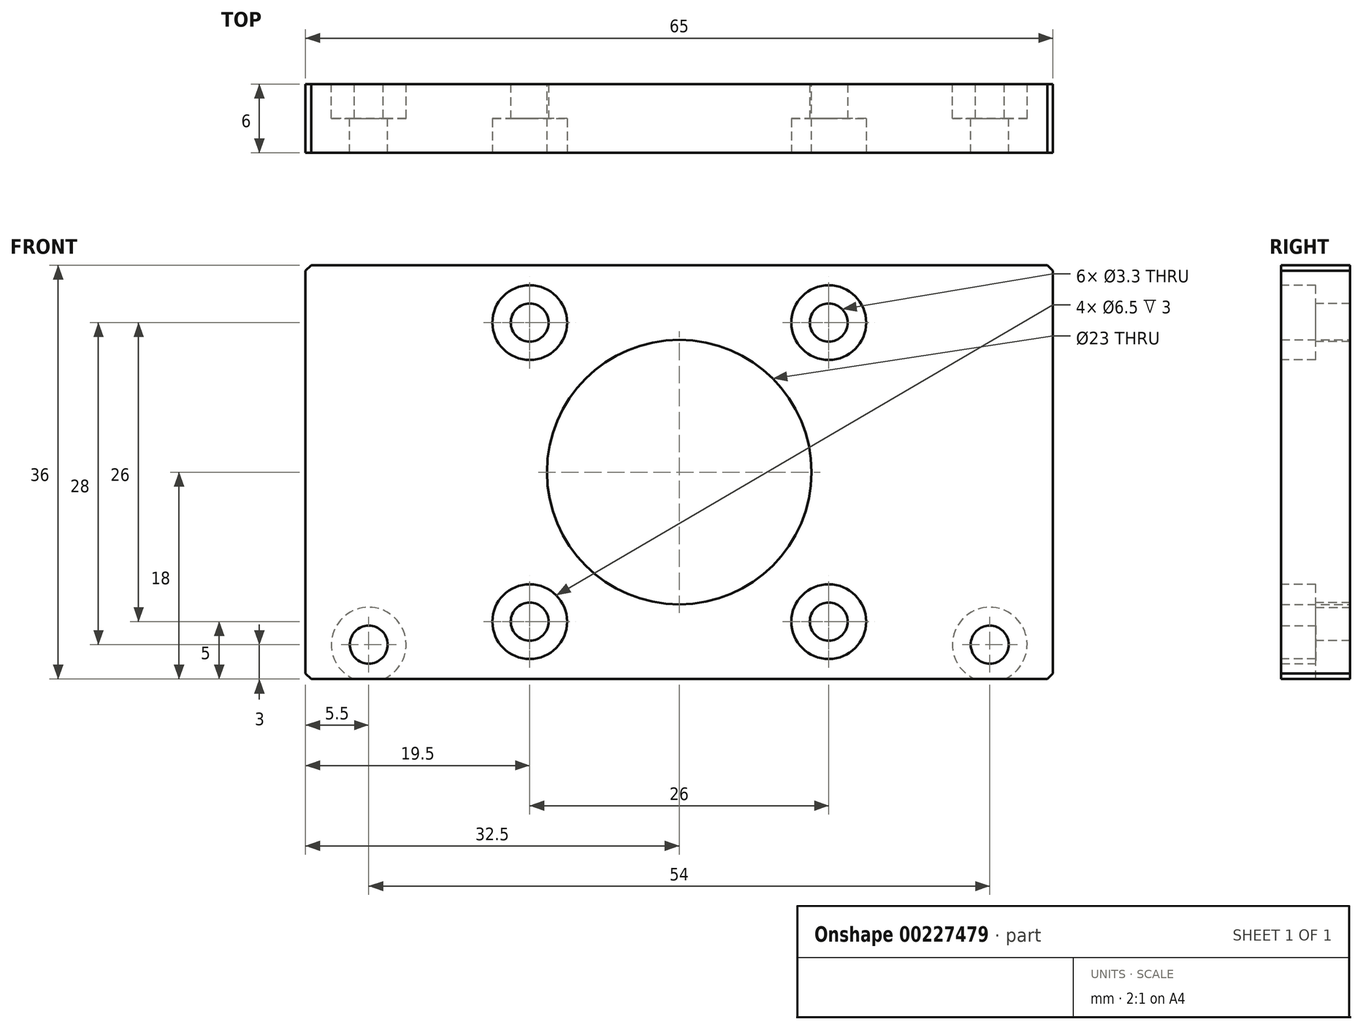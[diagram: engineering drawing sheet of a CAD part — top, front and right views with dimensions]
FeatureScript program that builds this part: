
annotation { "Feature Type Name" : "Feature", "Feature Type Description" : "" }
export const myFeature = defineFeature(function(context is Context, id is Id, definition is map)
    precondition{}
    {
        {
            var Q0;
            Q0=qCreatedBy(makeId("Front.planeOp"),FACE);
            var sketch = newSketch(context, id + "F0", { "sketchPlane" : qUnion([Q0])});
            skLineSegment(sketch, "E0.bottom", {"start": v(32.5, -18) * mm, "end": v(-32.5, -18) * mm});
            skLineSegment(sketch, "E0.top", {"start": v(32.5, 18) * mm, "end": v(-32.5, 18) * mm});
            skLineSegment(sketch, "E0.left", {"start": v(32.5, -18) * mm, "end": v(32.5, 18) * mm});
            skLineSegment(sketch, "E0.right", {"start": v(-32.5, -18) * mm, "end": v(-32.5, 18) * mm});
            skPoint(sketch, "E0.middle", {"position": v(0, 0) * mm});
            skCircle(sketch, "E1", {"center": v(0, 0) * mm, "radius": 11.5 * mm});
            skSolve(sketch);
        }
        {
            var Q0;
            Q0=makeQuery(id+"F0.imprint","IMPRINT",FACE,{"disambiguationData":[TD([[makeQuery(id+"F0.imprint","IMPRINT",EDGE,{"derivedFrom":sQuery(id+"F0.wireOp",EDGE,"E0.bottom")}),-1.0]])]});
            extrude(context, id + "F1", {"entities" : qUnion([Q0]), "depth" : 6 * mm});
        }
        {
            var Q0;
            Q0=makeQuery(id+"F1.opExtrude","CAP_FACE",FACE,{"disambiguationData":[OSD([sQuery(id+"F0.wireOp",EDGE,"E0.bottom"),sQuery(id+"F0.wireOp",EDGE,"E0.top"),sQuery(id+"F0.wireOp",EDGE,"E0.left"),sQuery(id+"F0.wireOp",EDGE,"E0.right")])],"isStart":false});
            var sketch = newSketch(context, id + "F2", { "sketchPlane" : qUnion([Q0])});
            skPoint(sketch, "E2", {"position": v(13, 13) * mm});
            skPoint(sketch, "E3.MirrorP", {"position": v(-13, 13) * mm});
            skPoint(sketch, "E4.MirrorP", {"position": v(13, -13) * mm});
            skPoint(sketch, "E5.MirrorP", {"position": v(-13, -13) * mm});
            skSolve(sketch);
        }
        {
            var Q0;
            Q0=sQuery(id+"F2.wireOp",VERTEX,"E2");
            var Q1;
            Q1=sQuery(id+"F2.wireOp",VERTEX,"E4.MirrorP");
            var Q2;
            Q2=sQuery(id+"F2.wireOp",VERTEX,"E5.MirrorP");
            var Q3;
            Q3=sQuery(id+"F2.wireOp",VERTEX,"E3.MirrorP");
            var Q4;
            Q4=makeQuery(id+"F1.opExtrude","SWEPT_BODY",BODY,{"disambiguationData":[OSD([sQuery(id+"F0.wireOp",EDGE,"E0.bottom"),sQuery(id+"F0.wireOp",EDGE,"E0.top"),sQuery(id+"F0.wireOp",EDGE,"E0.left"),sQuery(id+"F0.wireOp",EDGE,"E0.right")])]});
            hole(context, id + "F3", {"style" : HoleStyle.C_BORE, "endStyle" : HoleEndStyle.THROUGH, "standardTappedOrClearance" : lookupTablePath({ "standard" : "ISO", "fit" : "Normal", "size" : "M3", "type" : "Clearance" }), "standardBlindInLast" : lookupTablePath({ "fit" : "Standard", "standard" : "ISO", "size" : "M3", "type" : "Clearance" }), "holeDiameter" : 3.3 * mm, "cBoreDiameter" : 6.5 * mm, "cBoreDepth" : 3 * mm, "locations" : qUnion([Q0, Q1, Q2, Q3]), "scope" : qUnion([Q4]), "isTappedThrough" : true});
        }
        {
            var Q0;
            Q0=makeQuery(id+"F1.opExtrude","SWEPT_EDGE",EDGE,{"disambiguationData":[OSD([sQuery(id+"F0.wireOp",EDGE,"E0.top"),sQuery(id+"F0.wireOp",EDGE,"E0.right")])]});
            var Q1;
            Q1=makeQuery(id+"F1.opExtrude","SWEPT_EDGE",EDGE,{"disambiguationData":[OSD([sQuery(id+"F0.wireOp",EDGE,"E0.top"),sQuery(id+"F0.wireOp",EDGE,"E0.left")])]});
            var Q2;
            Q2=makeQuery(id+"F1.opExtrude","SWEPT_EDGE",EDGE,{"disambiguationData":[OSD([sQuery(id+"F0.wireOp",EDGE,"E0.bottom"),sQuery(id+"F0.wireOp",EDGE,"E0.left")])]});
            var Q3;
            Q3=makeQuery(id+"F1.opExtrude","SWEPT_EDGE",EDGE,{"disambiguationData":[OSD([sQuery(id+"F0.wireOp",EDGE,"E0.bottom"),sQuery(id+"F0.wireOp",EDGE,"E0.right")])]});
            chamfer(context, id + "F4", {"entities" : qUnion([Q0, Q1, Q2, Q3]), "width" : 0.5 * mm, "tangentPropagation" : true});
        }
        {
            var Q0;
            Q0=makeQuery(id+"F1.opExtrude","CAP_FACE",FACE,{"disambiguationData":[OSD([sQuery(id+"F0.wireOp",EDGE,"E0.bottom"),sQuery(id+"F0.wireOp",EDGE,"E0.top"),sQuery(id+"F0.wireOp",EDGE,"E0.left"),sQuery(id+"F0.wireOp",EDGE,"E0.right"),sQuery(id+"F0.wireOp",EDGE,"E1")])],"isStart":true});
            var sketch = newSketch(context, id + "F5", { "sketchPlane" : qUnion([Q0])});
            skPoint(sketch, "E6", {"position": v(-27, -15) * mm});
            skPoint(sketch, "E7.MirrorP", {"position": v(27, -15) * mm});
            skSolve(sketch);
        }
        {
            var Q0;
            Q0=sQuery(id+"F5.wireOp",VERTEX,"E6");
            var Q1;
            Q1=sQuery(id+"F5.wireOp",VERTEX,"E7.MirrorP");
            var Q2;
            Q2=makeQuery(id+"F1.opExtrude","SWEPT_BODY",BODY,{"disambiguationData":[OSD([sQuery(id+"F0.wireOp",EDGE,"E0.bottom"),sQuery(id+"F0.wireOp",EDGE,"E0.top"),sQuery(id+"F0.wireOp",EDGE,"E0.left"),sQuery(id+"F0.wireOp",EDGE,"E0.right"),sQuery(id+"F0.wireOp",EDGE,"E1")])]});
            hole(context, id + "F6", {"style" : HoleStyle.C_BORE, "endStyle" : HoleEndStyle.THROUGH, "standardTappedOrClearance" : lookupTablePath({ "standard" : "ISO", "fit" : "Normal", "size" : "M3", "type" : "Clearance" }), "standardBlindInLast" : lookupTablePath({ "fit" : "Standard", "standard" : "ISO", "size" : "M3", "type" : "Clearance" }), "holeDiameter" : 3.3 * mm, "cBoreDiameter" : 6.5 * mm, "cBoreDepth" : 3 * mm, "locations" : qUnion([Q0, Q1]), "scope" : qUnion([Q2]), "isTappedThrough" : true});
        }
    });
